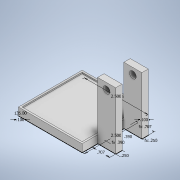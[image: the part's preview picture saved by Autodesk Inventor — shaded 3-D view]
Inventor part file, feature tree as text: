
AUTODESK INVENTOR PART (.ipt)
format: ipt  version: 2020 (Build 240168000, 168)  size: 147,968 bytes
history: native  units: in
note: dims shown in document units (in); Inventor stores cm internally (conversion verified against a paired STEP export)
features: extrude x3, sketch x2, hole x1
ambient origin geometry x8: Origin, YZ Plane, XZ Plane, XY Plane, X Axis, Y Axis, Z Axis, Center Point
bodies: Solid1 (feature_tree)
feature tree (6):
  sketch  "Sketch1"  dims[d3=0.0in d9=0.0in]
  extrude  "Extrusion1"  TaperAngle=0.0deg  [1 undecoded]
  extrude  "Extrusion2"  Depth=0.707in
  hole  "Hole1"  [1 undecoded]
  extrude  "Extrusion3"  TaperAngle=90.0deg  [1 undecoded]
  sketch  "Sketch3"  dims[d12=0.39in d15=0.707in d16=0.25in d18=90.0deg d19=0.266in d20=0.2in d21=0.507in d22=0.25in d23=0.5635in d24=0.25in d25=0.0in d26=0.1in d27=135.0deg d28=0.1in d29=0.3in d30=0.0in d11=1.0in d13=1.0in d14=0.15in d17=0.5635in]
note: 3 required parameter values undecoded (feature->parameter linkage not recoverable at this tier; creation-order binding heuristic only, values carry confidence <= 0.55)
